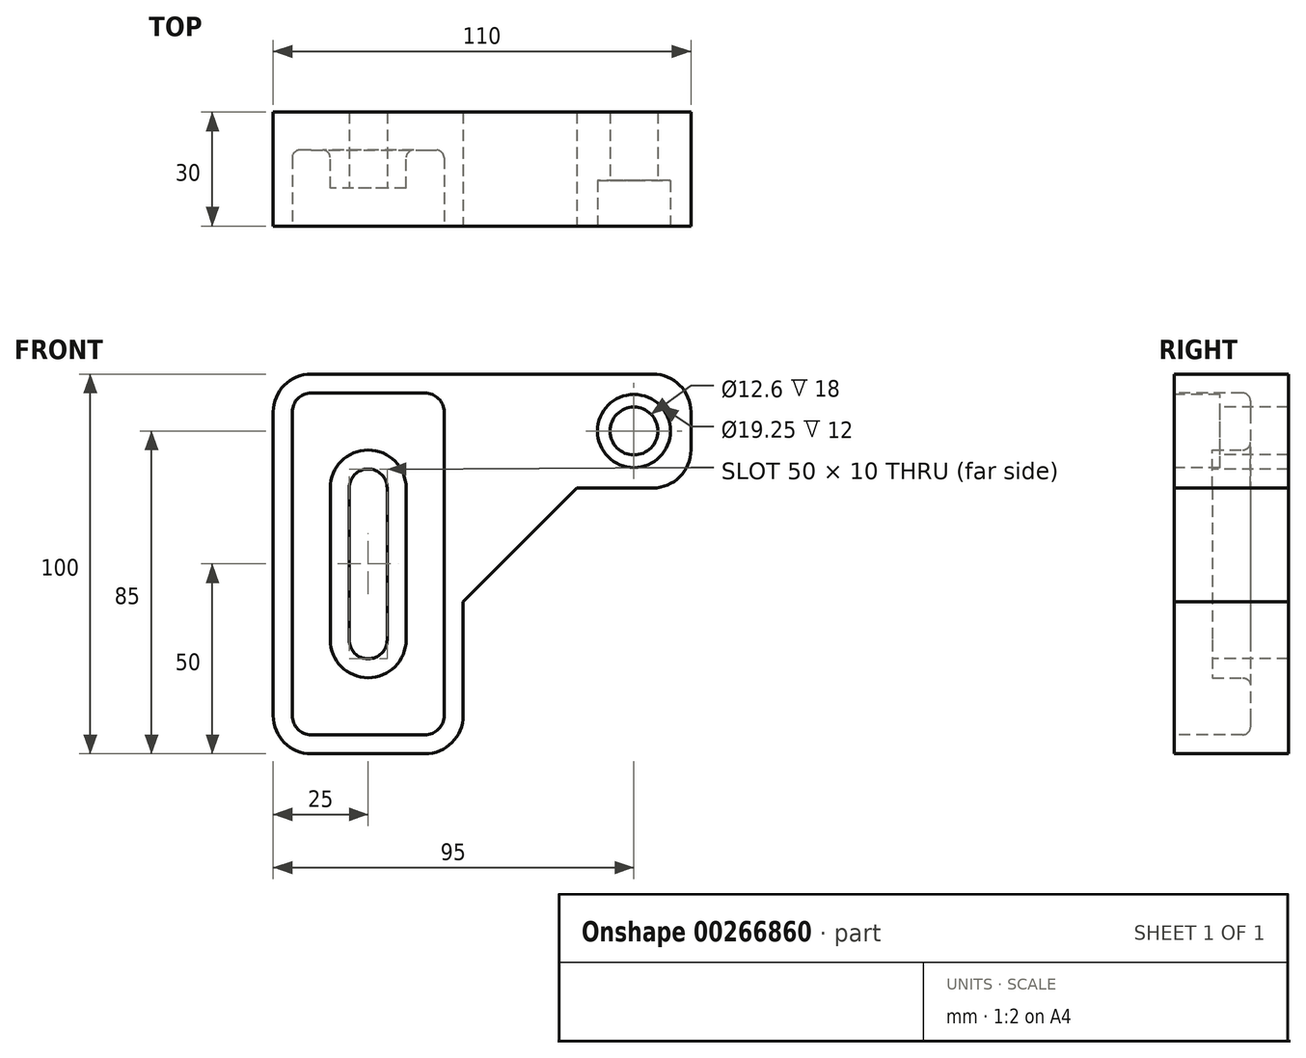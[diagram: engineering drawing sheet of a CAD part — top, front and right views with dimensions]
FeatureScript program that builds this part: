
annotation { "Feature Type Name" : "Feature", "Feature Type Description" : "" }
export const myFeature = defineFeature(function(context is Context, id is Id, definition is map)
    precondition{}
    {
        {
            var Q0;
            Q0=qCreatedBy(makeId("Front.planeOp"),FACE);
            var sketch = newSketch(context, id + "F0", { "sketchPlane" : qUnion([Q0])});
            skLineSegment(sketch, "E0", {"start": v(0, 0) * mm, "end": v(0, -30) * mm});
            skLineSegment(sketch, "E1", {"start": v(-10, -40) * mm, "end": v(-40, -40) * mm});
            skLineSegment(sketch, "E2", {"start": v(-50, -30) * mm, "end": v(-50, 50) * mm});
            skLineSegment(sketch, "E3", {"start": v(-40, 60) * mm, "end": v(50, 60) * mm});
            skLineSegment(sketch, "E4", {"start": v(0, 0) * mm, "end": v(30, 30) * mm});
            skLineSegment(sketch, "E5", {"start": v(30, 30) * mm, "end": v(50, 30) * mm});
            skLineSegment(sketch, "E6", {"start": v(60, 40) * mm, "end": v(60, 50) * mm});
            skPoint(sketch, "E7.visualSharp", {"position": v(-50, 60) * mm});
            skArc(sketch, "E7.filletArc", {"start": v(-40, 60) * mm, "mid": v(-47.07, 57.07) * mm, "end": v(-50, 50) * mm});
            skPoint(sketch, "E8.visualSharp", {"position": v(60, 60) * mm});
            skArc(sketch, "E8.filletArc", {"start": v(60, 50) * mm, "mid": v(57.07, 57.07) * mm, "end": v(50, 60) * mm});
            skPoint(sketch, "E9.visualSharp", {"position": v(60, 30) * mm});
            skArc(sketch, "E9.filletArc", {"start": v(50, 30) * mm, "mid": v(57.07, 32.93) * mm, "end": v(60, 40) * mm});
            skPoint(sketch, "E10.visualSharp", {"position": v(0, -40) * mm});
            skArc(sketch, "E10.filletArc", {"start": v(-10, -40) * mm, "mid": v(-2.93, -37.07) * mm, "end": v(0, -30) * mm});
            skPoint(sketch, "E11.visualSharp", {"position": v(-50, -40) * mm});
            skArc(sketch, "E11.filletArc", {"start": v(-50, -30) * mm, "mid": v(-47.07, -37.07) * mm, "end": v(-40, -40) * mm});
            skPoint(sketch, "E12", {"position": v(45, 45) * mm});
            skPoint(sketch, "E13", {"position": v(-25, 10) * mm});
            skPoint(sketch, "E14.visualSharp", {"position": v(-5, -35) * mm});
            skPoint(sketch, "E15.visualSharp", {"position": v(-45, -35) * mm});
            skSolve(sketch);
        }
        {
            var Q0;
            Q0 = qSketchRegion(id + "F0", true);
            extrude(context, id + "F1", {"entities" : qUnion([Q0]), "oppositeDirection" : true, "depth" : 30 * mm});
        }
        {
            var Q0;
            Q0=sQuery(id+"F0.wireOp",VERTEX,"E12");
            var Q1;
            Q1=makeQuery(id+"F1.opExtrude","SWEPT_BODY",BODY,{"disambiguationData":[OSD([sQuery(id+"F0.wireOp",EDGE,"E0"),sQuery(id+"F0.wireOp",EDGE,"E1"),sQuery(id+"F0.wireOp",EDGE,"E2"),sQuery(id+"F0.wireOp",EDGE,"E3"),sQuery(id+"F0.wireOp",EDGE,"E4"),sQuery(id+"F0.wireOp",EDGE,"E5"),sQuery(id+"F0.wireOp",EDGE,"E6"),sQuery(id+"F0.wireOp",EDGE,"E7.filletArc"),sQuery(id+"F0.wireOp",EDGE,"E8.filletArc"),sQuery(id+"F0.wireOp",EDGE,"E9.filletArc"),sQuery(id+"F0.wireOp",EDGE,"E10.filletArc"),sQuery(id+"F0.wireOp",EDGE,"E11.filletArc")])]});
            hole(context, id + "F2", {"style" : HoleStyle.C_BORE, "endStyle" : HoleEndStyle.THROUGH, "standardTappedOrClearance" : lookupTablePath({ "standard" : "ISO", "fit" : "Close", "size" : "M12", "type" : "Clearance" }), "standardBlindInLast" : lookupTablePath({ "fit" : "Close", "standard" : "ISO", "size" : "M12", "type" : "Clearance" }), "holeDiameter" : 12.6 * mm, "cBoreDiameter" : 19.25 * mm, "cBoreDepth" : 12 * mm, "tappedDepth" : 12 * mm, "tapClearance" : 3, "locations" : qUnion([Q0]), "scope" : qUnion([Q1])});
        }
        {
            var Q0;
            Q0=makeQuery(id+"F0.imprint","IMPRINT",FACE,{"disambiguationData":[TD([[makeQuery(id+"F0.imprint","IMPRINT",EDGE,{"derivedFrom":sQuery(id+"F0.wireOp",EDGE,"E0")}),-1.0]])]});
            var sketch = newSketch(context, id + "F3", { "sketchPlane" : qUnion([Q0])});
            skLineSegment(sketch, "E16.bottom", {"start": v(-40, 55) * mm, "end": v(-10, 55) * mm});
            skLineSegment(sketch, "E16.top", {"start": v(-40, -35) * mm, "end": v(-10, -35) * mm});
            skLineSegment(sketch, "E16.left", {"start": v(-45, 50) * mm, "end": v(-45, -30) * mm});
            skLineSegment(sketch, "E16.right", {"start": v(-5, 50) * mm, "end": v(-5, -30) * mm});
            skPoint(sketch, "E17.visualSharp", {"position": v(-45, 55) * mm});
            skArc(sketch, "E17.filletArc", {"start": v(-40, 55) * mm, "mid": v(-43.54, 53.54) * mm, "end": v(-45, 50) * mm});
            skPoint(sketch, "E18.visualSharp", {"position": v(-5, 55) * mm});
            skArc(sketch, "E18.filletArc", {"start": v(-5, 50) * mm, "mid": v(-6.46, 53.54) * mm, "end": v(-10, 55) * mm});
            skPoint(sketch, "E19.visualSharp", {"position": v(-5, -35) * mm});
            skArc(sketch, "E19.filletArc", {"start": v(-10, -35) * mm, "mid": v(-6.46, -33.54) * mm, "end": v(-5, -30) * mm});
            skPoint(sketch, "E20.visualSharp", {"position": v(-45, -35) * mm});
            skArc(sketch, "E20.filletArc", {"start": v(-45, -30) * mm, "mid": v(-43.54, -33.54) * mm, "end": v(-40, -35) * mm});
            skSolve(sketch);
        }
        {
            var Q0;
            Q0=makeQuery(id+"F3.imprint","IMPRINT",FACE,{"disambiguationData":[TD([[makeQuery(id+"F3.imprint","IMPRINT",EDGE,{"derivedFrom":sQuery(id+"F3.wireOp",EDGE,"E16.bottom")}),-1.0]])]});
            extrude(context, id + "F4", {"entities" : qUnion([Q0]), "operationType" : NewBodyOperationType.REMOVE, "oppositeDirection" : true, "depth" : 20 * mm});
        }
        {
            var Q0;
            Q0=qCreatedBy(makeId("Front.planeOp"),FACE);
            cPlane(context, id + "F5", {"entities" : qUnion([Q0]), "cplaneType" : CPlaneType.OFFSET, "offset" : 20 * mm, "oppositeDirection" : true, "width" : 150 * mm, "height" : 150 * mm});
        }
        {
            var Q0;
            Q0=qCreatedBy(id+"F5.planeOp",FACE);
            var sketch = newSketch(context, id + "F6", { "sketchPlane" : qUnion([Q0])});
            skArc(sketch, "E21", {"start": v(-15, 30) * mm, "mid": v(-25, 40) * mm, "end": v(-35, 30) * mm});
            skArc(sketch, "E22", {"start": v(-35, -10) * mm, "mid": v(-25, -20) * mm, "end": v(-15, -10) * mm});
            skLineSegment(sketch, "E23", {"start": v(-15, 30) * mm, "end": v(-15, -10) * mm});
            skLineSegment(sketch, "E24", {"start": v(-35, 30) * mm, "end": v(-35, -10) * mm});
            skSolve(sketch);
        }
        {
            var Q0;
            Q0 = qSketchRegion(id + "F6", true);
            extrude(context, id + "F7", {"entities" : qUnion([Q0]), "operationType" : NewBodyOperationType.ADD, "depth" : 10 * mm});
        }
        {
            var Q0;
            Q0=qCreatedBy(makeId("Front.planeOp"),FACE);
            cPlane(context, id + "F8", {"entities" : qUnion([Q0]), "cplaneType" : CPlaneType.OFFSET, "offset" : 10 * mm, "oppositeDirection" : true, "width" : 150 * mm, "height" : 150 * mm});
        }
        {
            var Q0;
            Q0=qCreatedBy(id+"F8.planeOp",FACE);
            var sketch = newSketch(context, id + "F9", { "sketchPlane" : qUnion([Q0])});
            skArc(sketch, "E25", {"start": v(-20, 30) * mm, "mid": v(-25, 35) * mm, "end": v(-30, 30) * mm});
            skArc(sketch, "E26", {"start": v(-30, -10) * mm, "mid": v(-25, -15) * mm, "end": v(-20, -10) * mm});
            skLineSegment(sketch, "E27", {"start": v(-30, 30) * mm, "end": v(-30, -10) * mm});
            skLineSegment(sketch, "E28", {"start": v(-20, 30) * mm, "end": v(-20, -10) * mm});
            skSolve(sketch);
        }
        {
            var Q0;
            Q0 = qSketchRegion(id + "F9", true);
            extrude(context, id + "F10", {"entities" : qUnion([Q0]), "operationType" : NewBodyOperationType.REMOVE, "endBound" : BoundingType.THROUGH_ALL, "oppositeDirection" : true, "depth" : 25 * mm});
        }
        {
            var Q0;
            Q0=makeQuery(id+"F4.boolean.opBoolean","COPY",FACE,{"derivedFrom":makeQuery(id+"F4.opExtrude","CAP_FACE",FACE,{"disambiguationData":[OSD([sQuery(id+"F3.wireOp",EDGE,"E16.bottom"),sQuery(id+"F3.wireOp",EDGE,"E16.top"),sQuery(id+"F3.wireOp",EDGE,"E16.left"),sQuery(id+"F3.wireOp",EDGE,"E16.right"),sQuery(id+"F3.wireOp",EDGE,"E17.filletArc"),sQuery(id+"F3.wireOp",EDGE,"E18.filletArc"),sQuery(id+"F3.wireOp",EDGE,"E19.filletArc"),sQuery(id+"F3.wireOp",EDGE,"E20.filletArc")])],"isStart":false})});
            fillet(context, id + "F11", {"entities" : qUnion([Q0]), "radius" : 2 * mm, "tangentPropagation" : true, "allowEdgeOverflow" : false});
        }
    });
